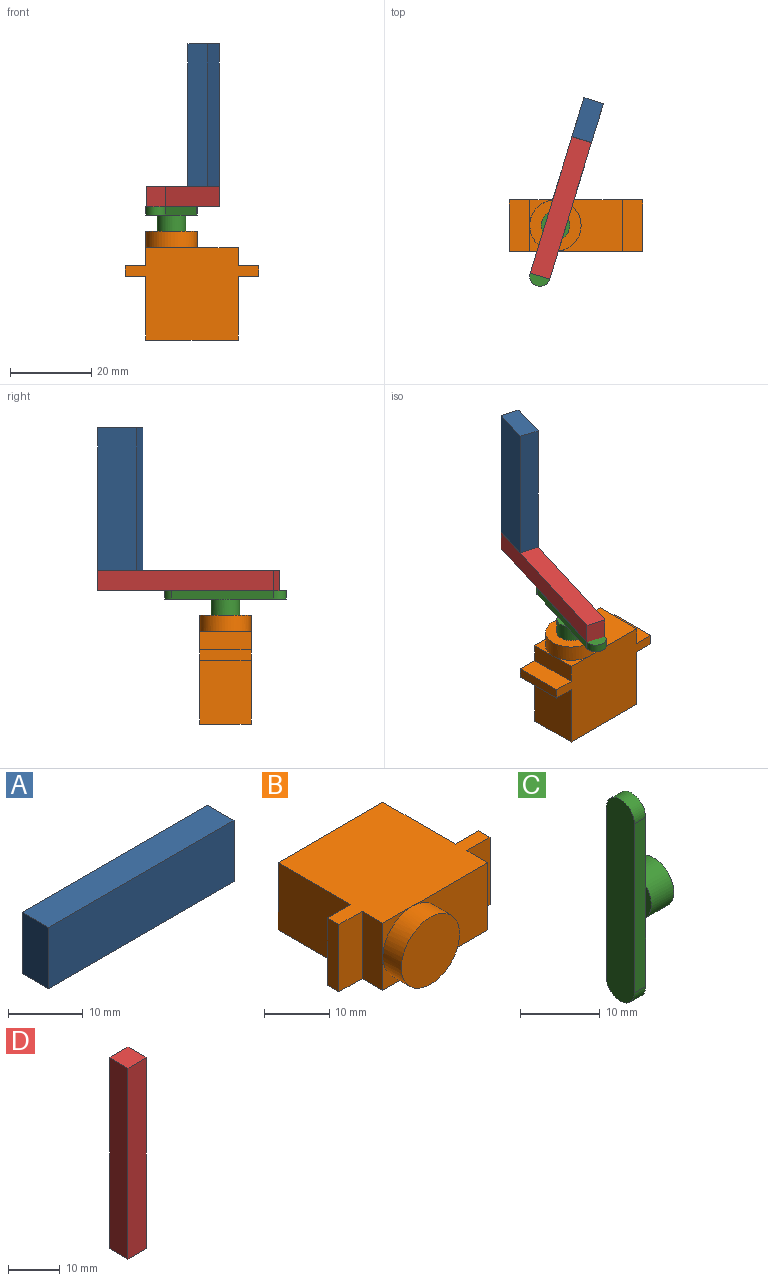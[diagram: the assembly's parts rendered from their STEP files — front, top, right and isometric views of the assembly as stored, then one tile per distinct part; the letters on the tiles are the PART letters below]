
ASSEMBLY  parts=4 mates=3
PART A: 6 faces, bbox 35x5x10 mm
  f0: plane 35x5mm, normal (0,0,-1), area 175mm2, adj f1,f3,f4,f5
  f1: plane 10x5mm, normal (1,0,0), area 50mm2, adj f0,f2,f4,f5
  f2: plane 35x5mm, normal (0,0,1), area 175mm2, adj f1,f3,f4,f5
  f3: plane 10x5mm, normal (-1,0,0), area 50mm2, adj f0,f2,f4,f5
  f4: plane 35x10mm, normal (0,1,0), area 350mm2, adj f0,f1,f2,f3
  f5: plane 35x10mm, normal (0,-1,0), area 350mm2, adj f0,f1,f2,f3
PART B: 18 faces, bbox 32.7x26.7x12.6 mm
  f0: plane 16.4x12.6mm, normal (0,-1,0), area 144.3mm2, adj f2,f8,f9,f16
  f1: plane 6.3x6.3mm, normal (0,-1,0), area 8.5mm2, adj f6,f8,f16
  f2: plane 12.6x4.5mm, normal (1,0,0), area 56.7mm2, adj f0,f8,f9,f13
  f3: plane 15.7x12.6mm, normal (-1,0,0), area 197.8mm2, adj f5,f8,f9,f11
  f4: plane 15.7x12.6mm, normal (1,0,0), area 197.8mm2, adj f5,f8,f9,f14
  f5: plane 22.7x12.6mm, normal (0,1,0), area 286mm2, adj f3,f4,f8,f9
  f6: plane 12.6x4.5mm, normal (-1,0,0), area 56.7mm2, adj f1,f7,f8,f9,f10
  f7: plane 6.3x6.3mm, normal (0,-1,0), area 8.5mm2, adj f6,f9,f16
  f8: plane 32.7x22.7mm, normal (0,0,1), area 540.3mm2, adj f0,f1,f2,f3,f4,f5,f6,f10
  f9: plane 32.7x22.7mm, normal (0,0,-1), area 540.3mm2, adj f0,f2,f3,f4,f5,f6,f7,f10
  f10: plane 12.6x5mm, normal (0,-1,0), area 63mm2, adj f6,f8,f9,f12
  f11: plane 12.6x5mm, normal (0,1,0), area 63mm2, adj f3,f8,f9,f12
  f12: plane 12.6x2.5mm, normal (-1,0,0), area 31.5mm2, adj f8,f9,f10,f11
  f13: plane 12.6x5mm, normal (0,-1,0), area 63mm2, adj f2,f8,f9,f15
  f14: plane 12.6x5mm, normal (0,1,0), area 63mm2, adj f4,f8,f9,f15
  f15: plane 12.6x2.5mm, normal (1,0,0), area 31.5mm2, adj f8,f9,f13,f14
  f16: cylinder r=6.3mm len=12.6mm, axis (0,1,0), area 158.3mm2, adj f0,f1,f7,f17
  f17: plane 12.6x12.6mm, normal (0,-1,0), area 124.7mm2, adj f16
PART C: 11 faces, bbox 6x7x31 mm
  f0: plane 13.05x5mm, normal (1,0,0), area 58.9mm2, adj f1,f2,f4,f8
  f1: cylinder r=2.5mm len=5mm, axis (-1,0,0), area 15.7mm2, adj f0,f2,f4,f6
  f2: plane 26x2mm, normal (0,-1,0), area 52mm2, adj f0,f1,f3,f5,f6,f7
  f3: cylinder r=2.5mm len=5mm, axis (-1,0,0), area 15.7mm2, adj f2,f4,f5,f6
  f4: plane 26x2mm, normal (0,1,0), area 52mm2, adj f0,f1,f3,f5,f6,f10
  f5: plane 13.05x5mm, normal (1,0,0), area 58.9mm2, adj f2,f3,f4,f8
  f6: plane 31x5mm, normal (-1,0,0), area 149.6mm2, adj f1,f2,f3,f4
  f7: plane 4.9x1mm, normal (-1,0,0), area 3.4mm2, adj f2,f8
  f8: cylinder r=3.5mm len=7mm, axis (-1,0,0), area 88mm2, adj f0,f5,f7,f9,f10
  f9: plane 7x7mm, normal (1,0,0), area 38.5mm2, adj f8
  f10: plane 4.9x1mm, normal (-1,0,0), area 3.4mm2, adj f4,f8
PART D: 6 faces, bbox 5x5x45 mm
  f0: plane 45x5mm, normal (1,0,0), area 225mm2, adj f1,f3,f4,f5
  f1: plane 5x5mm, normal (0,0,1), area 25mm2, adj f0,f2,f4,f5
  f2: plane 45x5mm, normal (-1,0,0), area 225mm2, adj f1,f3,f4,f5
  f3: plane 5x5mm, normal (0,0,-1), area 25mm2, adj f0,f2,f4,f5
  f4: plane 45x5mm, normal (0,-1,0), area 225mm2, adj f0,f1,f2,f3
  f5: plane 45x5mm, normal (0,1,0), area 225mm2, adj f0,f1,f2,f3
PLACE A rot(axis=(0.63,0.46,-0.63),130.3deg) t=(-17.82,-6.86,32.7)mm
PLACE B rot(axis=(-1,0,0),90deg) t=(0,0,0)mm
PLACE C rot(axis=(0.63,0.46,-0.63),130.3deg) t=(-17.82,-6.86,32.7)mm
PLACE D rot(axis=(-0.11,-0.7,0.7),168deg) t=(-22.6,-5.39,32.7)mm
MATE revolute C.f8 <-> B.f16  axis (0,0,-1) through (-16.4,6.3,26.7)mm
MATE fastened D.f5 <-> C.f1  axis (0,0,-1) through (-20.21,-6.13,32.7)mm
MATE fastened A.f1 <-> D.f4  axis (0,0,-1) through (-7.01,36.89,37.7)mm
